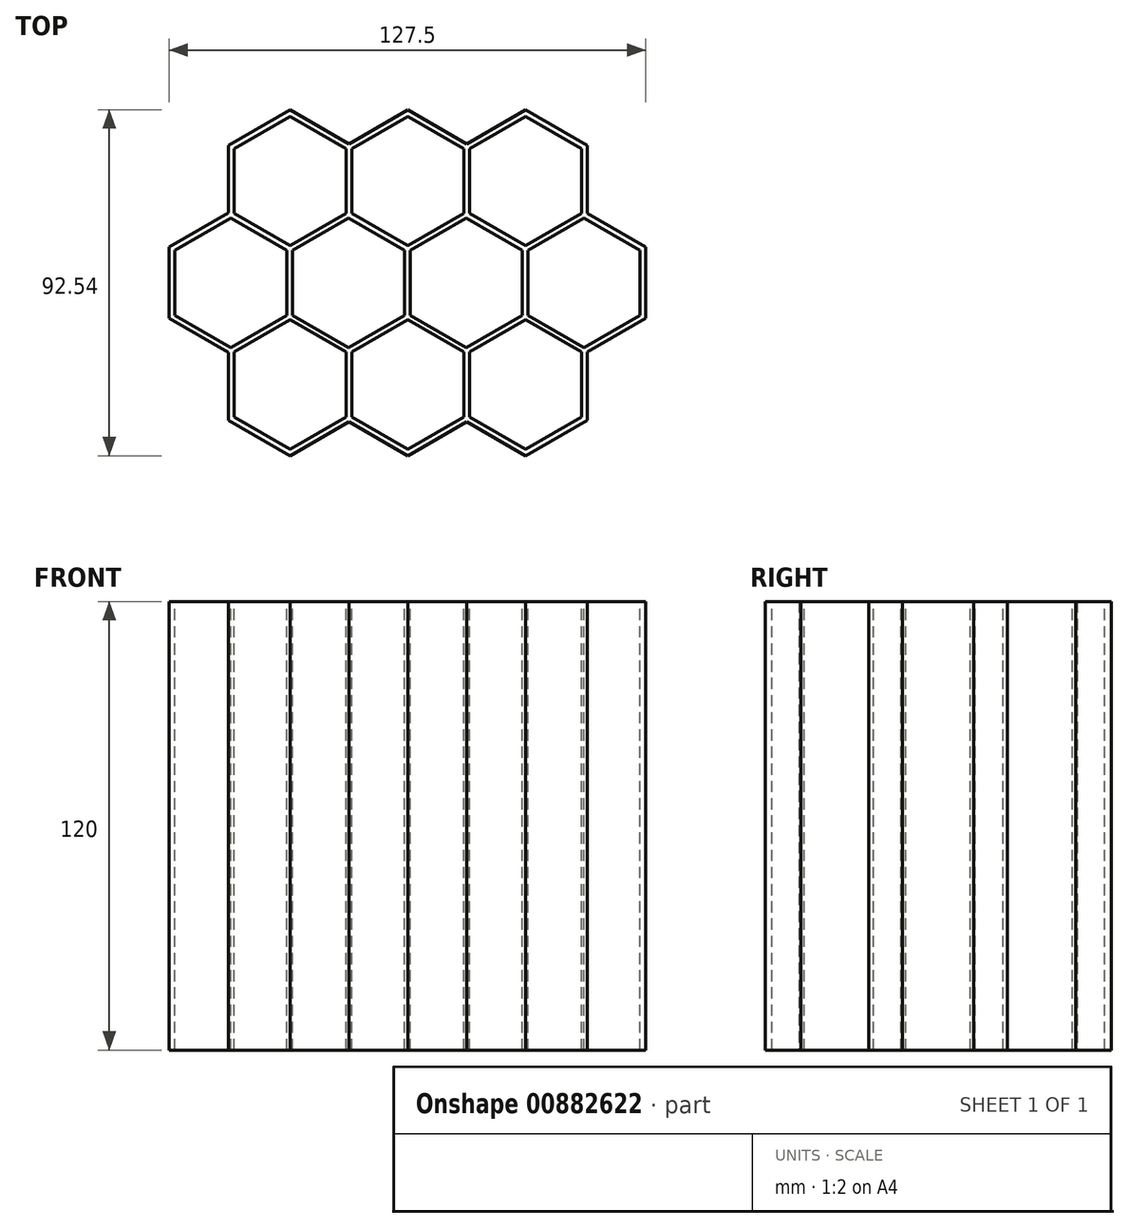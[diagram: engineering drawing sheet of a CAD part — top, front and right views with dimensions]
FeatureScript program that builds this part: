
annotation { "Feature Type Name" : "Feature", "Feature Type Description" : "" }
export const myFeature = defineFeature(function(context is Context, id is Id, definition is map)
    precondition{}
    {
        {
            var Q0;
            Q0=qCreatedBy(makeId("Top.planeOp"),FACE);
            var sketch = newSketch(context, id + "F0", { "sketchPlane" : qUnion([Q0])});
            skPoint(sketch, "E0.0.midPoint", {"position": v(-44.18, 14.23) * mm});
            skPoint(sketch, "E1.0.midPoint", {"position": v(-12.68, 14.23) * mm});
            skPoint(sketch, "E2.0.midPoint", {"position": v(18.82, 14.23) * mm});
            skPoint(sketch, "E3.0.midPoint", {"position": v(-60.04, -13) * mm});
            skPoint(sketch, "E4.0.midPoint", {"position": v(-36.68, -27.22) * mm});
            skLineSegment(sketch, "E5", {"start": v(-51.68, 46.27) * mm, "end": v(-35.93, 37.18) * mm});
            skLineSegment(sketch, "E6", {"start": v(-35.93, 37.18) * mm, "end": v(-20.18, 46.27) * mm});
            skLineSegment(sketch, "E7", {"start": v(-20.18, 46.27) * mm, "end": v(-4.43, 37.18) * mm});
            skLineSegment(sketch, "E8", {"start": v(-4.43, 37.18) * mm, "end": v(11.32, 46.27) * mm});
            skLineSegment(sketch, "E9", {"start": v(11.32, 46.27) * mm, "end": v(27.82, 36.74) * mm});
            skLineSegment(sketch, "E10", {"start": v(27.82, 36.74) * mm, "end": v(27.82, 18.56) * mm});
            skLineSegment(sketch, "E11", {"start": v(27.82, 18.56) * mm, "end": v(43.46, 9.53) * mm});
            skLineSegment(sketch, "E12", {"start": v(43.46, 9.53) * mm, "end": v(43.46, -9.53) * mm});
            skLineSegment(sketch, "E13", {"start": v(43.46, -9.53) * mm, "end": v(27.82, -18.56) * mm});
            skLineSegment(sketch, "E14", {"start": v(27.82, -18.56) * mm, "end": v(27.82, -36.74) * mm});
            skLineSegment(sketch, "E15", {"start": v(27.82, -36.74) * mm, "end": v(11.32, -46.27) * mm});
            skLineSegment(sketch, "E16", {"start": v(11.32, -46.27) * mm, "end": v(-4.43, -37.18) * mm});
            skLineSegment(sketch, "E17", {"start": v(-4.43, -37.18) * mm, "end": v(-20.18, -46.27) * mm});
            skLineSegment(sketch, "E18", {"start": v(-20.18, -46.27) * mm, "end": v(-35.93, -37.18) * mm});
            skLineSegment(sketch, "E19", {"start": v(-35.93, -37.18) * mm, "end": v(-51.68, -46.27) * mm});
            skLineSegment(sketch, "E20", {"start": v(-51.68, -46.27) * mm, "end": v(-68.18, -36.74) * mm});
            skLineSegment(sketch, "E21", {"start": v(-68.18, -36.74) * mm, "end": v(-68.18, -18.68) * mm});
            skLineSegment(sketch, "E22", {"start": v(-68.18, -18.68) * mm, "end": v(-84.04, -9.53) * mm});
            skLineSegment(sketch, "E23", {"start": v(-84.04, -9.53) * mm, "end": v(-84.04, 9.53) * mm});
            skLineSegment(sketch, "E24", {"start": v(-84.04, 9.53) * mm, "end": v(-68.18, 18.68) * mm});
            skLineSegment(sketch, "E25", {"start": v(-68.18, 18.68) * mm, "end": v(-68.18, 36.74) * mm});
            skLineSegment(sketch, "E26", {"start": v(-68.18, 36.74) * mm, "end": v(-51.68, 46.27) * mm});
            skPoint(sketch, "E27.orphan", {"position": v(-5.18, 18.56) * mm});
            skPoint(sketch, "E2.4.start.orphan", {"position": v(11.32, 44.54) * mm});
            skPoint(sketch, "E28.orphan", {"position": v(26.32, 18.56) * mm});
            skPoint(sketch, "E2.0.end.orphan", {"position": v(11.32, 9.9) * mm});
            skPoint(sketch, "E29.orphan", {"position": v(-20.18, 44.54) * mm});
            skPoint(sketch, "E1.0.end.orphan", {"position": v(-20.18, 9.9) * mm});
            skPoint(sketch, "E1.3.start.orphan", {"position": v(-35.18, 35.88) * mm});
            skPoint(sketch, "E0.4.end.orphan", {"position": v(-36.68, 35.88) * mm});
            skPoint(sketch, "E30.orphan", {"position": v(-67.54, 17.32) * mm});
            skPoint(sketch, "E31.orphan", {"position": v(-66.68, 18.56) * mm});
            skPoint(sketch, "E32.orphan", {"position": v(-51.68, 9.9) * mm});
            skPoint(sketch, "E0.5.end.orphan", {"position": v(-36.68, 18.56) * mm});
            skPoint(sketch, "E33.orphan", {"position": v(-51.68, 44.54) * mm});
            skPoint(sketch, "E3.cCircle.center.orphan", {"position": v(-67.54, 0) * mm});
            skPoint(sketch, "E34.orphan", {"position": v(-82.54, 8.66) * mm});
            skPoint(sketch, "E35.direction1.start.orphan", {"position": v(-52.54, -8.66) * mm});
            skPoint(sketch, "E36.orphan", {"position": v(-51.68, -9.9) * mm});
            skPoint(sketch, "E3.0.end.orphan", {"position": v(-67.54, -17.32) * mm});
            skPoint(sketch, "E37.orphan", {"position": v(-66.68, -18.56) * mm});
            skPoint(sketch, "E38.orphan", {"position": v(-36.68, -18.56) * mm});
            skPoint(sketch, "E39.orphan", {"position": v(-66.68, -35.88) * mm});
            skPoint(sketch, "E40.orphan", {"position": v(-51.68, -44.54) * mm});
            skPoint(sketch, "E4.1.start.orphan", {"position": v(-36.68, -35.88) * mm});
            skSolve(sketch);
        }
        {
            var Q0;
            Q0 = qSketchRegion(id + "F0", true);
            extrude(context, id + "F1", {"entities" : qUnion([Q0]), "depth" : 120 * mm, "offsetDistance" : 25 * mm});
        }
        {
            var Q0;
            Q0=makeQuery(id+"F1.opExtrude","CAP_FACE",FACE,{"disambiguationData":[OSD([sQuery(id+"F0.wireOp",EDGE,"E5"),sQuery(id+"F0.wireOp",EDGE,"E6"),sQuery(id+"F0.wireOp",EDGE,"E7"),sQuery(id+"F0.wireOp",EDGE,"E8"),sQuery(id+"F0.wireOp",EDGE,"E9"),sQuery(id+"F0.wireOp",EDGE,"E10"),sQuery(id+"F0.wireOp",EDGE,"E11"),sQuery(id+"F0.wireOp",EDGE,"E12"),sQuery(id+"F0.wireOp",EDGE,"E13"),sQuery(id+"F0.wireOp",EDGE,"E14"),sQuery(id+"F0.wireOp",EDGE,"E15"),sQuery(id+"F0.wireOp",EDGE,"E16"),sQuery(id+"F0.wireOp",EDGE,"E17"),sQuery(id+"F0.wireOp",EDGE,"E18"),sQuery(id+"F0.wireOp",EDGE,"E19"),sQuery(id+"F0.wireOp",EDGE,"E20"),sQuery(id+"F0.wireOp",EDGE,"E21"),sQuery(id+"F0.wireOp",EDGE,"E22"),sQuery(id+"F0.wireOp",EDGE,"E23"),sQuery(id+"F0.wireOp",EDGE,"E24"),sQuery(id+"F0.wireOp",EDGE,"E25"),sQuery(id+"F0.wireOp",EDGE,"E26")])],"isStart":false});
            var sketch = newSketch(context, id + "F2", { "sketchPlane" : qUnion([Q0])});
            skLineSegment(sketch, "E41.0", {"start": v(-68.18, 36.74) * mm, "end": v(-51.68, 46.27) * mm});
            skCircle(sketch, "E42.cCircle", {"center": v(-51.68, 27.22) * mm, "radius": 15 * mm, "construction": true});
            skLineSegment(sketch, "E42.0", {"start": v(-66.68, 35.88) * mm, "end": v(-66.68, 18.56) * mm});
            skLineSegment(sketch, "E42.1", {"start": v(-51.68, 44.54) * mm, "end": v(-66.68, 35.88) * mm});
            skLineSegment(sketch, "E42.2", {"start": v(-36.68, 35.88) * mm, "end": v(-51.68, 44.54) * mm});
            skLineSegment(sketch, "E42.3", {"start": v(-36.68, 18.56) * mm, "end": v(-36.68, 35.88) * mm});
            skLineSegment(sketch, "E42.4", {"start": v(-51.68, 9.9) * mm, "end": v(-36.68, 18.56) * mm});
            skLineSegment(sketch, "E42.5", {"start": v(-66.68, 18.56) * mm, "end": v(-51.68, 9.9) * mm});
            skPoint(sketch, "E42.0.midPoint", {"position": v(-66.68, 27.22) * mm});
            skCircle(sketch, "E43.cCircle", {"center": v(-67.54, 0) * mm, "radius": 15 * mm, "construction": true});
            skLineSegment(sketch, "E43.0", {"start": v(-52.54, -8.66) * mm, "end": v(-67.54, -17.32) * mm});
            skLineSegment(sketch, "E43.1", {"start": v(-67.54, -17.32) * mm, "end": v(-82.54, -8.66) * mm});
            skLineSegment(sketch, "E43.2", {"start": v(-82.54, -8.66) * mm, "end": v(-82.54, 8.66) * mm});
            skLineSegment(sketch, "E43.3", {"start": v(-82.54, 8.66) * mm, "end": v(-67.54, 17.32) * mm});
            skLineSegment(sketch, "E43.4", {"start": v(-67.54, 17.32) * mm, "end": v(-52.54, 8.66) * mm});
            skLineSegment(sketch, "E43.5", {"start": v(-52.54, 8.66) * mm, "end": v(-52.54, -8.66) * mm});
            skPoint(sketch, "E43.0.midPoint", {"position": v(-60.04, -13) * mm});
            skCircle(sketch, "E44.cCircle", {"center": v(-51.68, -27.22) * mm, "radius": 15 * mm, "construction": true});
            skLineSegment(sketch, "E44.0", {"start": v(-36.68, -35.88) * mm, "end": v(-51.68, -44.54) * mm});
            skLineSegment(sketch, "E44.1", {"start": v(-51.68, -44.54) * mm, "end": v(-66.68, -35.88) * mm});
            skLineSegment(sketch, "E44.2", {"start": v(-66.68, -35.88) * mm, "end": v(-66.68, -18.56) * mm});
            skLineSegment(sketch, "E44.3", {"start": v(-66.68, -18.56) * mm, "end": v(-51.68, -9.9) * mm});
            skLineSegment(sketch, "E44.4", {"start": v(-51.68, -9.9) * mm, "end": v(-36.68, -18.56) * mm});
            skLineSegment(sketch, "E44.5", {"start": v(-36.68, -18.56) * mm, "end": v(-36.68, -35.88) * mm});
            skPoint(sketch, "E44.0.midPoint", {"position": v(-44.18, -40.2) * mm});
            skLineSegment(sketch, "E45.1.0.0", {"start": v(-5.18, 18.56) * mm, "end": v(-5.18, 35.88) * mm});
            skLineSegment(sketch, "E45.1.0.1", {"start": v(-20.18, 9.9) * mm, "end": v(-5.18, 18.56) * mm});
            skLineSegment(sketch, "E45.1.0.2", {"start": v(-35.18, 18.56) * mm, "end": v(-20.18, 9.9) * mm});
            skLineSegment(sketch, "E45.1.0.3", {"start": v(-5.18, 35.88) * mm, "end": v(-20.18, 44.54) * mm});
            skLineSegment(sketch, "E45.1.0.4", {"start": v(-20.18, 44.54) * mm, "end": v(-35.18, 35.88) * mm});
            skLineSegment(sketch, "E45.1.0.5", {"start": v(-35.18, 35.88) * mm, "end": v(-35.18, 18.56) * mm});
            skLineSegment(sketch, "E45.1.0.6", {"start": v(-20.18, -9.9) * mm, "end": v(-5.18, -18.56) * mm});
            skLineSegment(sketch, "E45.1.0.7", {"start": v(-5.18, -18.56) * mm, "end": v(-5.18, -35.88) * mm});
            skLineSegment(sketch, "E45.1.0.8", {"start": v(-5.18, -35.88) * mm, "end": v(-20.18, -44.54) * mm});
            skLineSegment(sketch, "E45.1.0.9", {"start": v(-35.18, -18.56) * mm, "end": v(-20.18, -9.9) * mm});
            skLineSegment(sketch, "E45.1.0.10", {"start": v(-35.18, -35.88) * mm, "end": v(-35.18, -18.56) * mm});
            skLineSegment(sketch, "E45.1.0.11", {"start": v(-20.18, -44.54) * mm, "end": v(-35.18, -35.88) * mm});
            skLineSegment(sketch, "E45.2.0.0", {"start": v(26.32, 18.56) * mm, "end": v(26.32, 35.88) * mm});
            skLineSegment(sketch, "E45.2.0.1", {"start": v(11.32, 9.9) * mm, "end": v(26.32, 18.56) * mm});
            skLineSegment(sketch, "E45.2.0.2", {"start": v(-3.68, 18.56) * mm, "end": v(11.32, 9.9) * mm});
            skLineSegment(sketch, "E45.2.0.3", {"start": v(26.32, 35.88) * mm, "end": v(11.32, 44.54) * mm});
            skLineSegment(sketch, "E45.2.0.4", {"start": v(11.32, 44.54) * mm, "end": v(-3.68, 35.88) * mm});
            skLineSegment(sketch, "E45.2.0.5", {"start": v(-3.68, 35.88) * mm, "end": v(-3.68, 18.56) * mm});
            skLineSegment(sketch, "E45.2.0.6", {"start": v(11.32, -9.9) * mm, "end": v(26.32, -18.56) * mm});
            skLineSegment(sketch, "E45.2.0.7", {"start": v(26.32, -18.56) * mm, "end": v(26.32, -35.88) * mm});
            skLineSegment(sketch, "E45.2.0.8", {"start": v(26.32, -35.88) * mm, "end": v(11.32, -44.54) * mm});
            skLineSegment(sketch, "E45.2.0.9", {"start": v(-3.68, -18.56) * mm, "end": v(11.32, -9.9) * mm});
            skLineSegment(sketch, "E45.2.0.10", {"start": v(-3.68, -35.88) * mm, "end": v(-3.68, -18.56) * mm});
            skLineSegment(sketch, "E45.2.0.11", {"start": v(11.32, -44.54) * mm, "end": v(-3.68, -35.88) * mm});
            skLineSegment(sketch, "E45.direction1", {"start": v(-36.68, 18.56) * mm, "end": v(-5.18, 18.56) * mm, "construction": true});
            skLineSegment(sketch, "E46.1.0.0", {"start": v(-21.04, 8.66) * mm, "end": v(-21.04, -8.66) * mm});
            skLineSegment(sketch, "E46.1.0.1", {"start": v(-36.04, 17.32) * mm, "end": v(-21.04, 8.66) * mm});
            skLineSegment(sketch, "E46.1.0.2", {"start": v(-51.04, 8.66) * mm, "end": v(-36.04, 17.32) * mm});
            skLineSegment(sketch, "E46.1.0.3", {"start": v(-51.04, -8.66) * mm, "end": v(-51.04, 8.66) * mm});
            skLineSegment(sketch, "E46.1.0.4", {"start": v(-36.04, -17.32) * mm, "end": v(-51.04, -8.66) * mm});
            skLineSegment(sketch, "E46.1.0.5", {"start": v(-21.04, -8.66) * mm, "end": v(-36.04, -17.32) * mm});
            skLineSegment(sketch, "E46.2.0.0", {"start": v(10.46, 8.66) * mm, "end": v(10.46, -8.66) * mm});
            skLineSegment(sketch, "E46.2.0.1", {"start": v(-4.54, 17.32) * mm, "end": v(10.46, 8.66) * mm});
            skLineSegment(sketch, "E46.2.0.2", {"start": v(-19.54, 8.66) * mm, "end": v(-4.54, 17.32) * mm});
            skLineSegment(sketch, "E46.2.0.3", {"start": v(-19.54, -8.66) * mm, "end": v(-19.54, 8.66) * mm});
            skLineSegment(sketch, "E46.2.0.4", {"start": v(-4.54, -17.32) * mm, "end": v(-19.54, -8.66) * mm});
            skLineSegment(sketch, "E46.2.0.5", {"start": v(10.46, -8.66) * mm, "end": v(-4.54, -17.32) * mm});
            skLineSegment(sketch, "E46.3.0.0", {"start": v(41.96, 8.66) * mm, "end": v(41.96, -8.66) * mm});
            skLineSegment(sketch, "E46.3.0.1", {"start": v(26.96, 17.32) * mm, "end": v(41.96, 8.66) * mm});
            skLineSegment(sketch, "E46.3.0.2", {"start": v(11.96, 8.66) * mm, "end": v(26.96, 17.32) * mm});
            skLineSegment(sketch, "E46.3.0.3", {"start": v(11.96, -8.66) * mm, "end": v(11.96, 8.66) * mm});
            skLineSegment(sketch, "E46.3.0.4", {"start": v(26.96, -17.32) * mm, "end": v(11.96, -8.66) * mm});
            skLineSegment(sketch, "E46.3.0.5", {"start": v(41.96, -8.66) * mm, "end": v(26.96, -17.32) * mm});
            skLineSegment(sketch, "E46.direction1", {"start": v(-52.54, -8.66) * mm, "end": v(-21.04, -8.66) * mm, "construction": true});
            skSolve(sketch);
        }
        {
            var Q0;
            Q0 = qSketchRegion(id + "F2", true);
            extrude(context, id + "F3", {"entities" : qUnion([Q0]), "operationType" : NewBodyOperationType.REMOVE, "endBound" : BoundingType.THROUGH_ALL, "oppositeDirection" : true, "depth" : 25 * mm, "offsetDistance" : 25 * mm});
        }
    });
